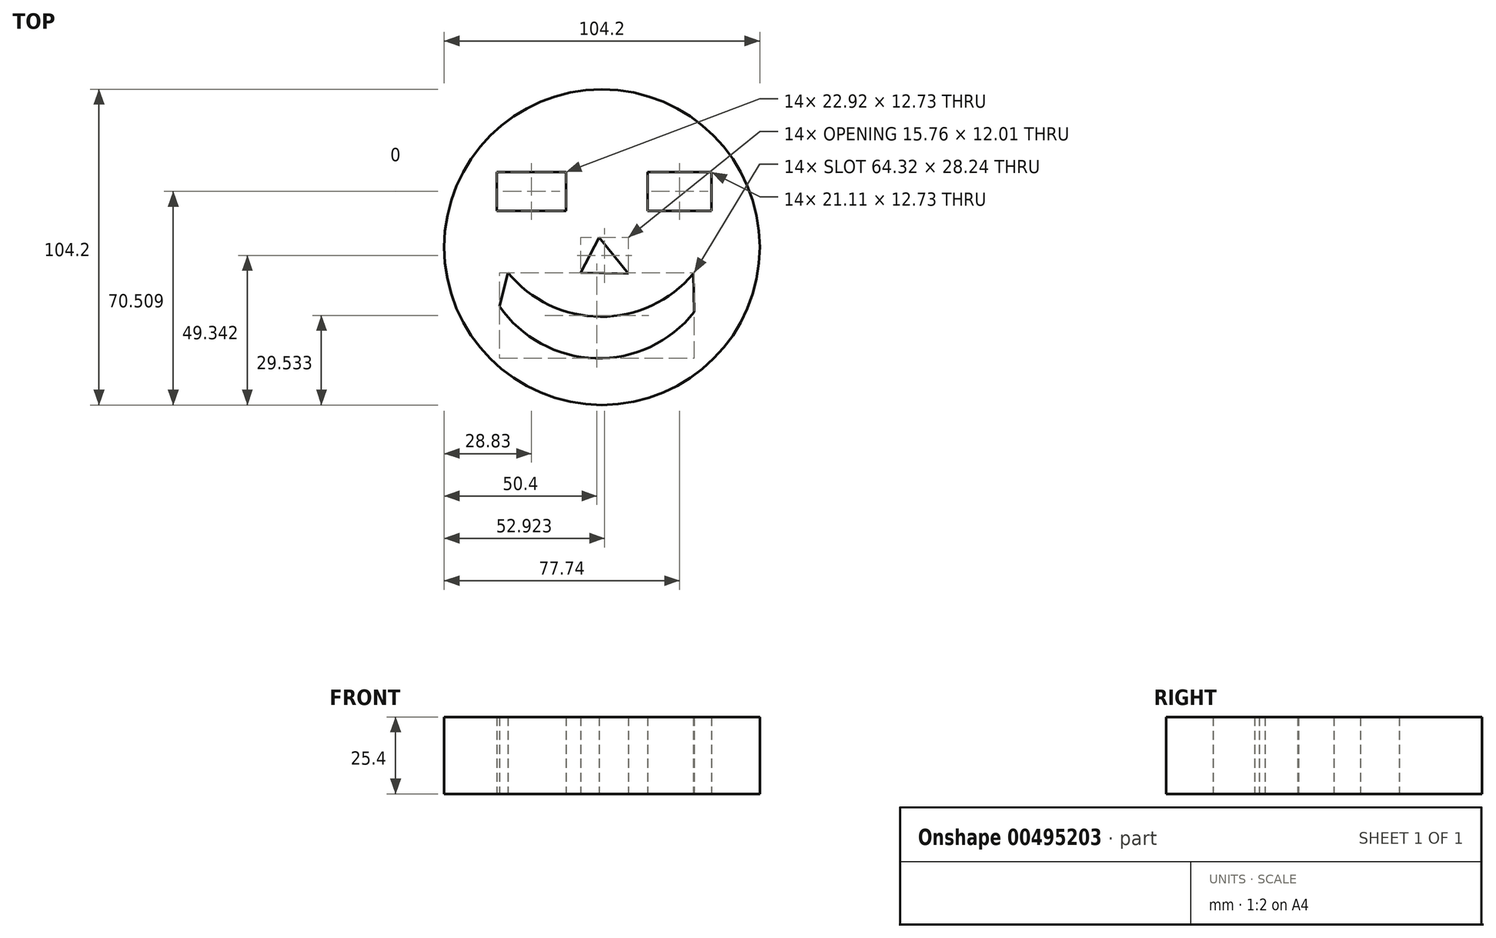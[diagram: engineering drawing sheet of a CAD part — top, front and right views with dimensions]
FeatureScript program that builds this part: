
annotation { "Feature Type Name" : "Feature", "Feature Type Description" : "" }
export const myFeature = defineFeature(function(context is Context, id is Id, definition is map)
    precondition{}
    {
        {
            var Q0;
            Q0=qCreatedBy(makeId("Top.planeOp"),FACE);
            var sketch = newSketch(context, id + "F0", { "sketchPlane" : qUnion([Q0])});
            skCircle(sketch, "E0", {"center": v(0, 0) * mm, "radius": 52.1 * mm});
            skLineSegment(sketch, "E1.bottom", {"start": v(-34.73, 24.78) * mm, "end": v(-11.8, 24.78) * mm});
            skLineSegment(sketch, "E1.top", {"start": v(-34.73, 12.04) * mm, "end": v(-11.8, 12.04) * mm});
            skLineSegment(sketch, "E1.left", {"start": v(-34.73, 24.78) * mm, "end": v(-34.73, 12.04) * mm});
            skLineSegment(sketch, "E1.right", {"start": v(-11.8, 24.78) * mm, "end": v(-11.8, 12.04) * mm});
            skLineSegment(sketch, "E2.bottom", {"start": v(15.09, 12.04) * mm, "end": v(36.2, 12.04) * mm});
            skLineSegment(sketch, "E2.top", {"start": v(15.09, 24.78) * mm, "end": v(36.2, 24.78) * mm});
            skLineSegment(sketch, "E2.left", {"start": v(15.09, 12.04) * mm, "end": v(15.09, 24.78) * mm});
            skLineSegment(sketch, "E2.right", {"start": v(36.2, 12.04) * mm, "end": v(36.2, 24.78) * mm});
            skArc(sketch, "E3", {"start": v(-33.86, -19.48) * mm, "mid": v(-2.18, -36.69) * mm, "end": v(30.46, -21.37) * mm});
            skArc(sketch, "E4", {"start": v(-31.02, -8.45) * mm, "mid": v(-0.51, -22.95) * mm, "end": v(30.15, -8.76) * mm});
            skLineSegment(sketch, "E5", {"start": v(-31.02, -8.45) * mm, "end": v(-33.86, -19.48) * mm});
            skLineSegment(sketch, "E6", {"start": v(30.15, -8.76) * mm, "end": v(30.46, -21.37) * mm});
            skLineSegment(sketch, "E7", {"start": v(-1, 3.24) * mm, "end": v(-7.06, -8.45) * mm});
            skLineSegment(sketch, "E8", {"start": v(-7.06, -8.45) * mm, "end": v(8.7, -8.76) * mm});
            skCircle(sketch, "E9", {"center": v(-24.09, 19.3) * mm, "radius": 3.8 * mm});
            skCircle(sketch, "E10", {"center": v(25.64, 19.6) * mm, "radius": 3.8 * mm});
            skPoint(sketch, "E10.centerSnap0", {"position": v(25.64, 12.04) * mm});
            skLineSegment(sketch, "E11", {"start": v(8.7, -8.76) * mm, "end": v(-1, 3.24) * mm});
            skArc(sketch, "E12", {"start": v(-7.46, 27.05) * mm, "mid": v(-22.78, 32.05) * mm, "end": v(-38.02, 26.82) * mm});
            skArc(sketch, "E13", {"start": v(39.42, 27.05) * mm, "mid": v(24.26, 32.07) * mm, "end": v(9.1, 27.05) * mm});
            skSolve(sketch);
        }
        {
            var Q0;
            Q0 = qSketchRegion(id + "F0", true);
            extrude(context, id + "F1", {"entities" : qUnion([Q0]), "depth" : 25.4 * mm});
        }
    });
